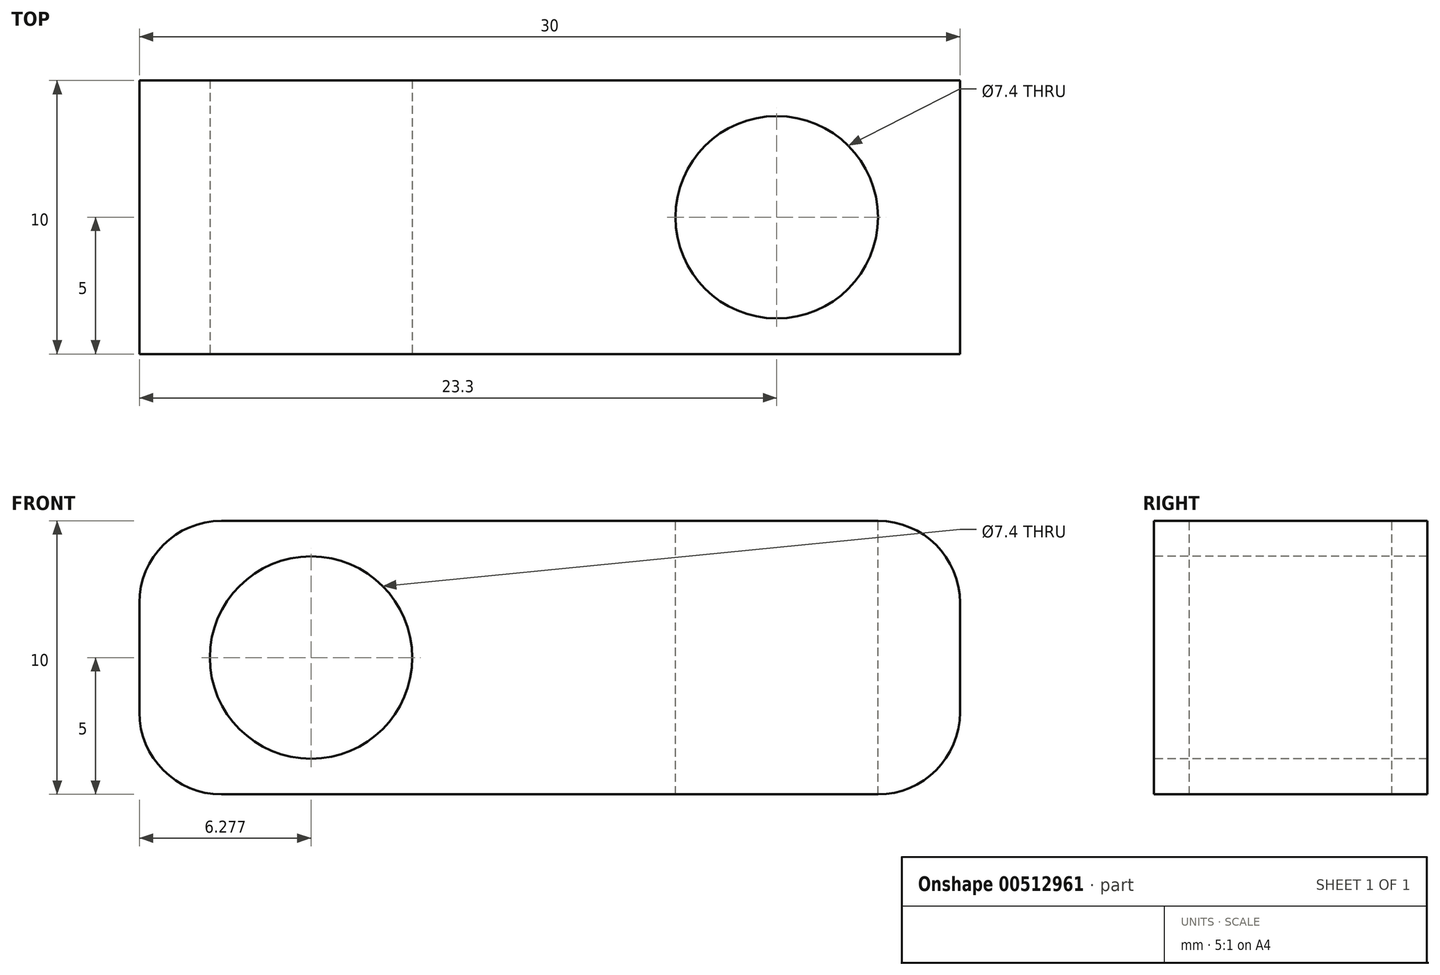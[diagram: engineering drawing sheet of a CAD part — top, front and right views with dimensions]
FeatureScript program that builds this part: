
annotation { "Feature Type Name" : "Feature", "Feature Type Description" : "" }
export const myFeature = defineFeature(function(context is Context, id is Id, definition is map)
    precondition{}
    {
        {
            var Q0;
            Q0=qCreatedBy(makeId("Top.planeOp"),FACE);
            var sketch = newSketch(context, id + "F0", { "sketchPlane" : qUnion([Q0])});
            skLineSegment(sketch, "E0.bottom", {"start": v(-15, 5) * mm, "end": v(15, 5) * mm});
            skLineSegment(sketch, "E0.top", {"start": v(-15, -5) * mm, "end": v(15, -5) * mm});
            skLineSegment(sketch, "E0.left", {"start": v(-15, 5) * mm, "end": v(-15, -5) * mm});
            skLineSegment(sketch, "E0.right", {"start": v(15, 5) * mm, "end": v(15, -5) * mm});
            skPoint(sketch, "E0.middle", {"position": v(0, 0) * mm});
            skSolve(sketch);
        }
        {
            var Q0;
            Q0=makeQuery(id+"F0.imprint","IMPRINT",FACE,{"disambiguationData":[TD([[makeQuery(id+"F0.imprint","IMPRINT",EDGE,{"derivedFrom":sQuery(id+"F0.wireOp",EDGE,"E0.bottom")}),-1.0]])]});
            extrude(context, id + "F1", {"entities" : qUnion([Q0]), "depth" : 10 * mm, "offsetDistance" : 25 * mm});
        }
        {
            var Q0;
            Q0=makeQuery(id+"F1.opExtrude","CAP_FACE",FACE,{"disambiguationData":[OSD([sQuery(id+"F0.wireOp",EDGE,"E0.bottom"),sQuery(id+"F0.wireOp",EDGE,"E0.top"),sQuery(id+"F0.wireOp",EDGE,"E0.left"),sQuery(id+"F0.wireOp",EDGE,"E0.right")])],"isStart":false});
            var sketch = newSketch(context, id + "F2", { "sketchPlane" : qUnion([Q0])});
            skCircle(sketch, "E1", {"center": v(8.3, 0) * mm, "radius": 3.7 * mm});
            skSolve(sketch);
        }
        {
            var Q0;
            Q0 = qSketchRegion(id + "F2", true);
            extrude(context, id + "F3", {"entities" : qUnion([Q0]), "operationType" : NewBodyOperationType.REMOVE, "endBound" : BoundingType.UP_TO_NEXT, "oppositeDirection" : true, "depth" : 25 * mm, "offsetDistance" : 25 * mm});
        }
        {
            var Q0;
            Q0=makeQuery(id+"F1.opExtrude","SWEPT_FACE",FACE,{"disambiguationData":[OSD([sQuery(id+"F0.wireOp",EDGE,"E0.top")])]});
            var sketch = newSketch(context, id + "F4", { "sketchPlane" : qUnion([Q0])});
            skCircle(sketch, "E2", {"center": v(-8.72, 5) * mm, "radius": 3.7 * mm});
            skSolve(sketch);
        }
        {
            var Q0;
            Q0 = qSketchRegion(id + "F4", true);
            extrude(context, id + "F5", {"entities" : qUnion([Q0]), "operationType" : NewBodyOperationType.REMOVE, "endBound" : BoundingType.UP_TO_NEXT, "oppositeDirection" : true, "depth" : 25 * mm, "offsetDistance" : 25 * mm});
        }
        {
            var Q0;
            Q0=makeQuery(id+"F1.opExtrude","CAP_EDGE",EDGE,{"disambiguationData":[OSD([sQuery(id+"F0.wireOp",EDGE,"E0.left")])],"isStart":false});
            var Q1;
            Q1=makeQuery(id+"F1.opExtrude","CAP_EDGE",EDGE,{"disambiguationData":[OSD([sQuery(id+"F0.wireOp",EDGE,"E0.right")])],"isStart":false});
            var Q2;
            Q2=makeQuery(id+"F1.opExtrude","CAP_EDGE",EDGE,{"disambiguationData":[OSD([sQuery(id+"F0.wireOp",EDGE,"E0.right")])],"isStart":true});
            var Q3;
            Q3=makeQuery(id+"F1.opExtrude","CAP_EDGE",EDGE,{"disambiguationData":[OSD([sQuery(id+"F0.wireOp",EDGE,"E0.left")])],"isStart":true});
            fillet(context, id + "F6", {"entities" : qUnion([Q0, Q1, Q2, Q3]), "radius" : 3 * mm, "tangentPropagation" : true, "allowEdgeOverflow" : false});
        }
    });
